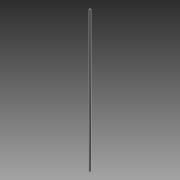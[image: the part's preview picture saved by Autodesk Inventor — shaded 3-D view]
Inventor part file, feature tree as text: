
AUTODESK INVENTOR PART (.ipt)
format: ipt  version: 2013 (Build 170138000, 138)  size: 73,216 bytes
history: native  units: mm
features: extrude x1, sketch x1
ambient origin geometry x8: Origin, YZ Plane, XZ Plane, XY Plane, X Axis, Y Axis, Z Axis, Center Point
bodies: Solid1 (feature_tree)
feature tree (2):
  extrude  "Extrusion1"  Depth=407.0mm TaperAngle=0.0deg
  sketch  "Sketch1"  dims[d0=5.0mm d2=407.0mm d3=0.0mm]
